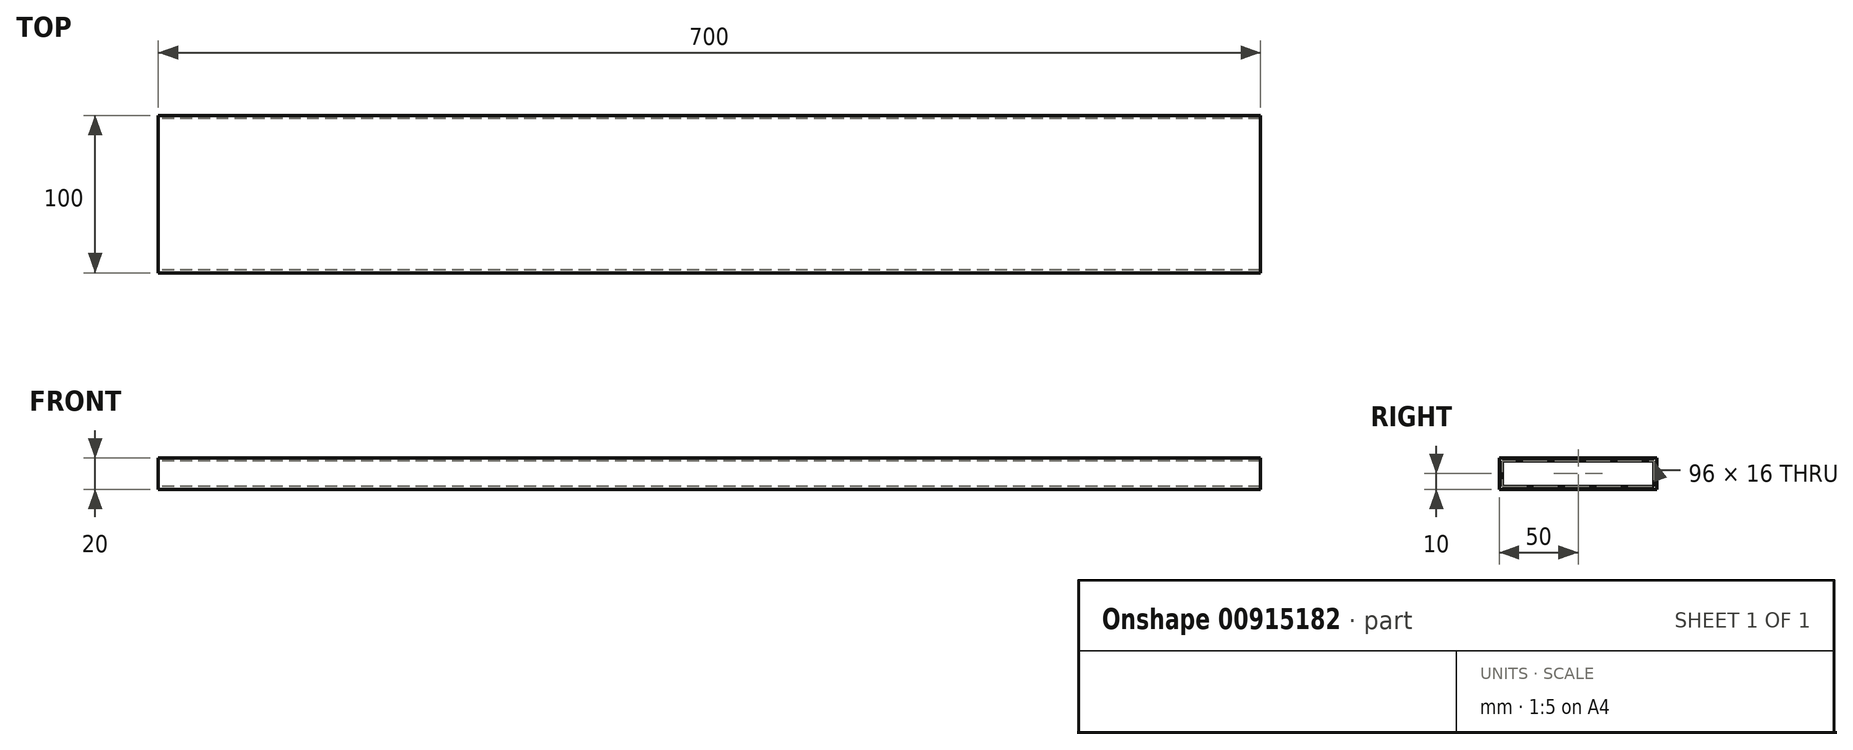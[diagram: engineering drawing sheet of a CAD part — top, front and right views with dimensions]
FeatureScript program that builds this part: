
annotation { "Feature Type Name" : "Feature", "Feature Type Description" : "" }
export const myFeature = defineFeature(function(context is Context, id is Id, definition is map)
    precondition{}
    {
        {
            var Q0;
            Q0=qCreatedBy(makeId("Right.planeOp"),FACE);
            var sketch = newSketch(context, id + "F0", { "sketchPlane" : qUnion([Q0])});
            skLineSegment(sketch, "E0.bottom", {"start": v(-48, 18) * mm, "end": v(48, 18) * mm});
            skLineSegment(sketch, "E0.top", {"start": v(-48, 2) * mm, "end": v(48, 2) * mm});
            skLineSegment(sketch, "E0.left", {"start": v(-48, 18) * mm, "end": v(-48, 2) * mm});
            skLineSegment(sketch, "E0.right", {"start": v(48, 18) * mm, "end": v(48, 2) * mm});
            skLineSegment(sketch, "E1.0", {"start": v(-50, 20) * mm, "end": v(50, 20) * mm});
            skLineSegment(sketch, "E1.1", {"start": v(-50, 20) * mm, "end": v(-50, 0) * mm});
            skLineSegment(sketch, "E1.2", {"start": v(-50, 0) * mm, "end": v(50, 0) * mm});
            skLineSegment(sketch, "E1.3", {"start": v(50, 20) * mm, "end": v(50, 0) * mm});
            skSolve(sketch);
        }
        {
            var Q0;
            Q0=makeQuery(id+"F0.imprint","IMPRINT",FACE,{"disambiguationData":[TD([[makeQuery(id+"F0.imprint","IMPRINT",EDGE,{"derivedFrom":sQuery(id+"F0.wireOp",EDGE,"E0.bottom")}),1.0]])]});
            extrude(context, id + "F1", {"entities" : qUnion([Q0]), "depth" : 700 * mm, "offsetDistance" : 25 * mm});
        }
    });
